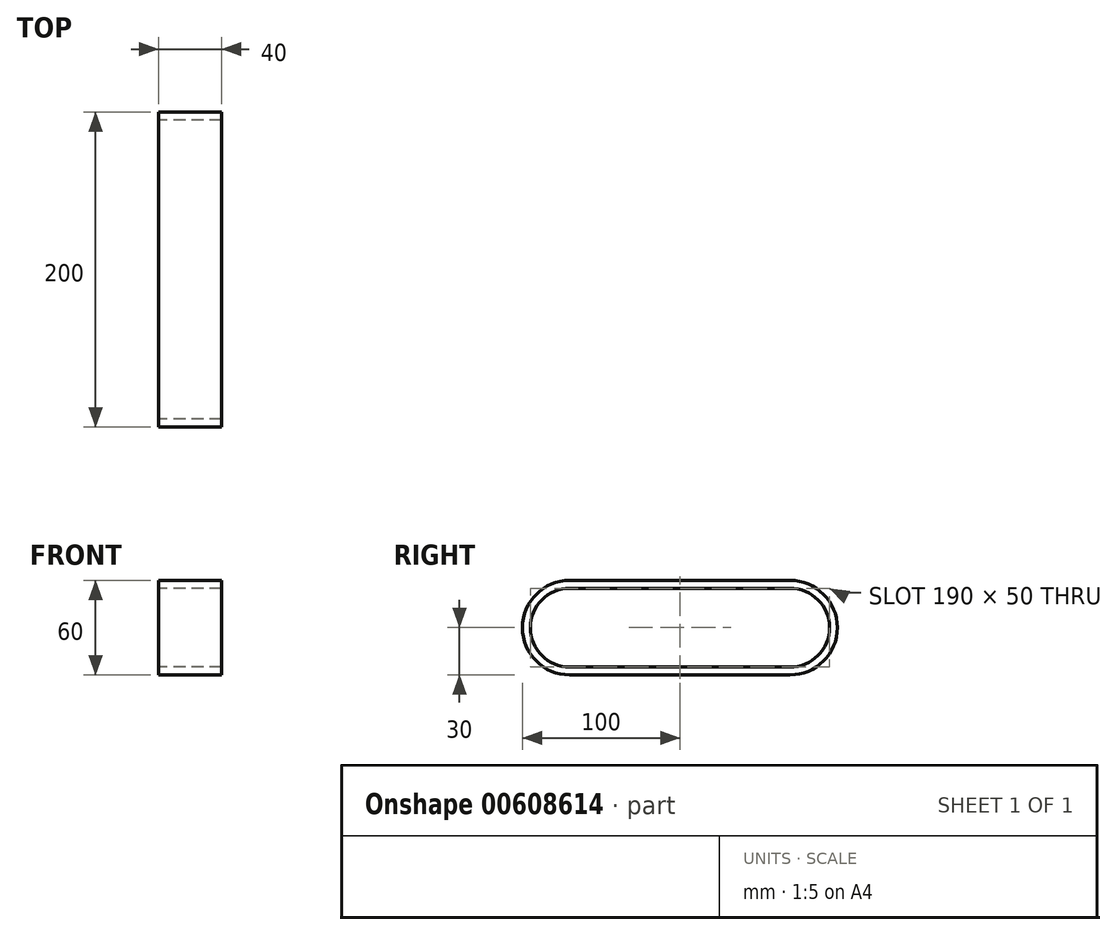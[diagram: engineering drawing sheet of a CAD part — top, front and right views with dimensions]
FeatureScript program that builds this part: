
annotation { "Feature Type Name" : "Feature", "Feature Type Description" : "" }
export const myFeature = defineFeature(function(context is Context, id is Id, definition is map)
    precondition{}
    {
        {
            var Q0;
            Q0=qCreatedBy(makeId("Right.planeOp"),FACE);
            var sketch = newSketch(context, id + "F0", { "sketchPlane" : qUnion([Q0])});
            skArc(sketch, "E0", {"start": v(0, 25) * mm, "mid": v(-25, 0) * mm, "end": v(0, -25) * mm});
            skArc(sketch, "E1", {"start": v(140, -25) * mm, "mid": v(165, 0) * mm, "end": v(140, 25) * mm});
            skLineSegment(sketch, "E2", {"start": v(0, 25) * mm, "end": v(140, 25) * mm});
            skLineSegment(sketch, "E3", {"start": v(0, -25) * mm, "end": v(140, -25) * mm});
            skLineSegment(sketch, "E4.0", {"start": v(0, -30) * mm, "end": v(140, -30) * mm});
            skArc(sketch, "E4.1", {"start": v(0, 30) * mm, "mid": v(-30, 0) * mm, "end": v(0, -30) * mm});
            skLineSegment(sketch, "E4.2", {"start": v(0, 30) * mm, "end": v(140, 30) * mm});
            skArc(sketch, "E4.3", {"start": v(140, -30) * mm, "mid": v(170, 0) * mm, "end": v(140, 30) * mm});
            skSolve(sketch);
        }
        {
            var Q0;
            Q0=makeQuery(id+"F0.imprint","IMPRINT",FACE,{"disambiguationData":[TD([[makeQuery(id+"F0.imprint","IMPRINT",EDGE,{"derivedFrom":sQuery(id+"F0.wireOp",EDGE,"E0")}),-1.0]])]});
            extrude(context, id + "F1", {"entities" : qUnion([Q0]), "depth" : 40 * mm, "offsetDistance" : 25 * mm});
        }
    });
